# Revit family: Access_Door-ACUDOR_Air_Tight_ADWT
name_source: partatom
category: Doors
revit_build: Autodesk Revit 2017 (Build: 20171027_0315(x64)
units: mm (PartAtom-declared; Revit-internal decimal feet)

## family parameters
Cut with Voids When Loaded = No
Host = Face
Room Calculation Point = No
Shared = No

## types (7) — shared parameters
Analytic Construction = <None>
Code = -24 "
Default Elevation = 48 "
Description = AIRTIGHT / WATERTIGHT
Manufacturer = ACUDOR
Material Finish = Metal - Acudor - Stainless - Polished
URL = www.acudor.com
zero-valued in all types: Thickness

## per-type parameters (varying)
| type | Height | Width |
| ADWT-1212 | 14.75 " | 14.75 " |
| ADWT-1414 | 16.75 " | 16.75 " |
| ADWT-1818 | 20.75 " | 20.75 " |
| ADWT-2424 | 26.75 " | 26.75 " |
| ADWT-2436 | 38.75 " | 26.75 " |
| ADWT-3030 | 32.75 " | 32.75 " |
| ADWT-3048 | 50.75 " | 32.75 " |

note: column(s) folded — value = type name in every type: Model

## geometry (parser evidence)
native form markers: Blend x4, Sweep x7
no freeform markers — native parametric forms only
